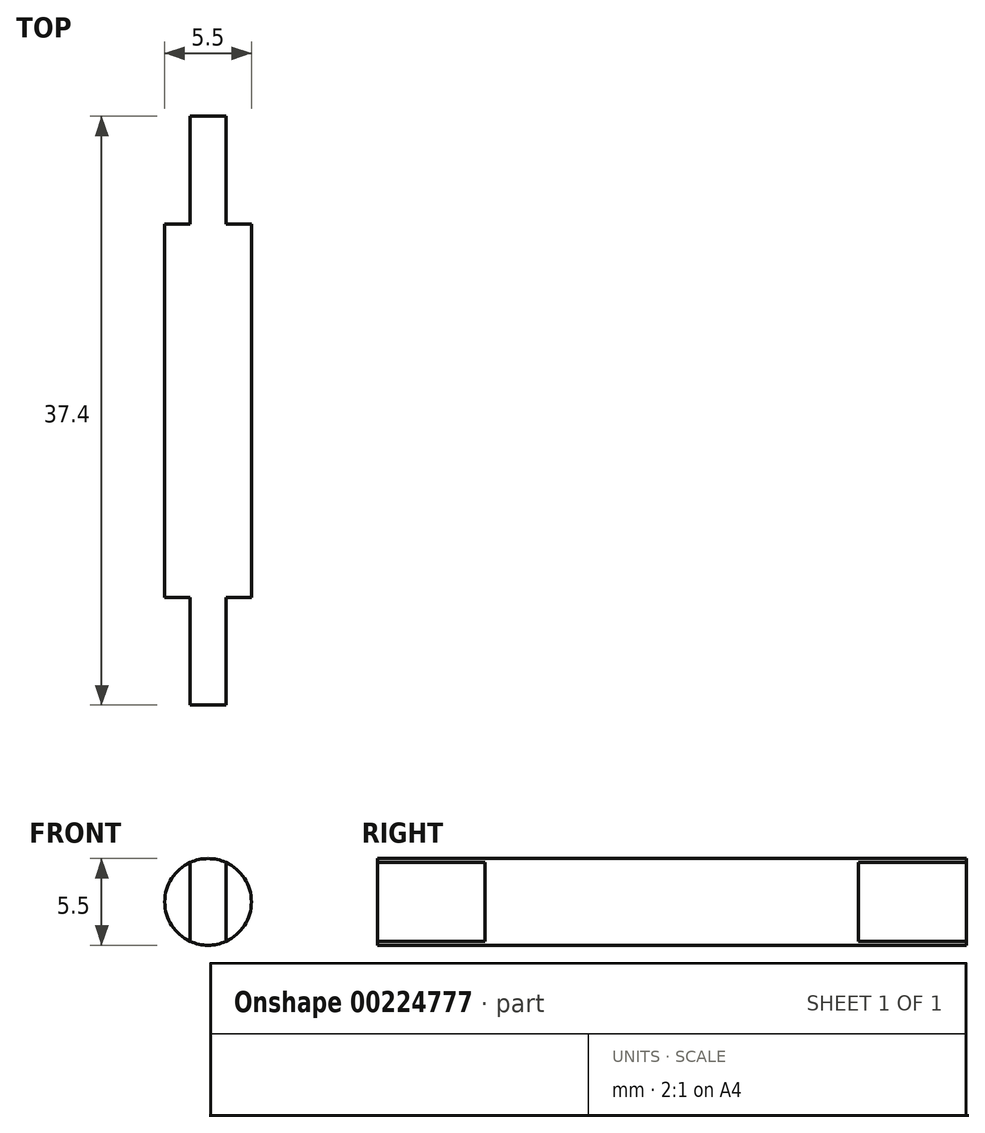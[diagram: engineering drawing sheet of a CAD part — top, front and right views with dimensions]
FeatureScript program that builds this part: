
annotation { "Feature Type Name" : "Feature", "Feature Type Description" : "" }
export const myFeature = defineFeature(function(context is Context, id is Id, definition is map)
    precondition{}
    {
        {
            var Q0;
            Q0=qCreatedBy(makeId("Front.planeOp"),FACE);
            var sketch = newSketch(context, id + "F0", { "sketchPlane" : qUnion([Q0])});
            skCircle(sketch, "E0", {"center": v(0, 0) * mm, "radius": 2.75 * mm});
            skLineSegment(sketch, "E1", {"start": v(-1.13, 2.5) * mm, "end": v(-1.13, -2.5) * mm});
            skLineSegment(sketch, "E2", {"start": v(0, 2.75) * mm, "end": v(0, -2.75) * mm, "construction": true});
            skLineSegment(sketch, "E3.MirrorCS", {"start": v(1.13, 2.5) * mm, "end": v(1.13, -2.5) * mm});
            skSolve(sketch);
        }
        {
            var Q0;
            {var subQ0=sQuery(id+"F0.wireOp",EDGE,"E1");Q0=makeQuery(id+"F0.imprint","IMPRINT",FACE,{"disambiguationData":[TD([[makeQuery(id+"F0.imprint","IMPRINT",EDGE,{"derivedFrom":subQ0}),1.0]])]});}
            extrude(context, id + "F1", {"entities" : qUnion([Q0]), "depth" : 37.4 * mm, "hasSecondDirection" : true, "secondDirectionOppositeDirection" : true, "secondDirectionDepth" : 25 * mm, "symmetric" : true});
        }
        {
            var Q0;
            {var subQ0=sQuery(id+"F0.wireOp",EDGE,"E1");Q0=makeQuery(id+"F0.imprint","IMPRINT",FACE,{"disambiguationData":[TD([[makeQuery(id+"F0.imprint","IMPRINT",EDGE,{"derivedFrom":subQ0}),-1.0]])]});}
            var Q1;
            {var subQ0=sQuery(id+"F0.wireOp",EDGE,"E3.MirrorCS");Q1=makeQuery(id+"F0.imprint","IMPRINT",FACE,{"disambiguationData":[TD([[makeQuery(id+"F0.imprint","IMPRINT",EDGE,{"derivedFrom":subQ0}),1.0]])]});}
            extrude(context, id + "F2", {"entities" : qUnion([Q0, Q1]), "operationType" : NewBodyOperationType.ADD, "depth" : 23.7 * mm, "symmetric" : true});
        }
    });
